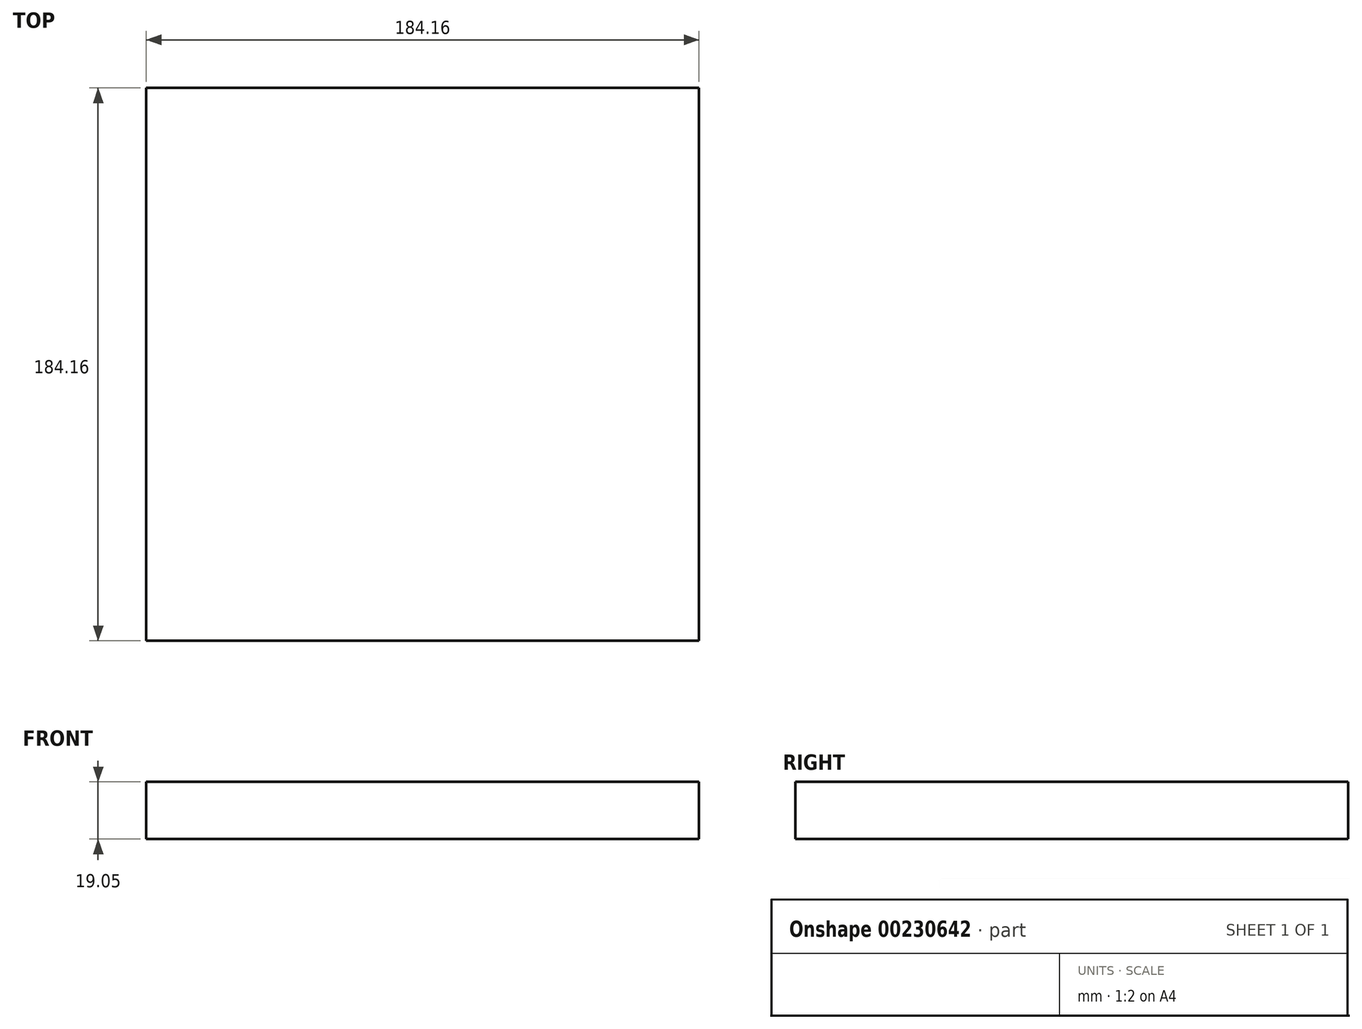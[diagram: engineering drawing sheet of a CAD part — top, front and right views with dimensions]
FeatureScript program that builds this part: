
annotation { "Feature Type Name" : "Feature", "Feature Type Description" : "" }
export const myFeature = defineFeature(function(context is Context, id is Id, definition is map)
    precondition{}
    {
        {
            var Q0;
            Q0=qCreatedBy(makeId("Top.planeOp"),FACE);
            var sketch = newSketch(context, id + "F0", { "sketchPlane" : qUnion([Q0])});
            skLineSegment(sketch, "E0.bottom", {"start": v(92.07, 92.08) * mm, "end": v(-92.07, 92.08) * mm});
            skLineSegment(sketch, "E0.top", {"start": v(92.08, -92.08) * mm, "end": v(-92.07, -92.08) * mm});
            skLineSegment(sketch, "E0.left", {"start": v(92.08, 92.08) * mm, "end": v(92.08, -92.08) * mm});
            skLineSegment(sketch, "E0.right", {"start": v(-92.07, 92.08) * mm, "end": v(-92.07, -92.08) * mm});
            skPoint(sketch, "E0.middle", {"position": v(0, 0) * mm});
            skSolve(sketch);
        }
        {
            var Q0;
            Q0 = qSketchRegion(id + "F0", true);
            extrude(context, id + "F1", {"entities" : qUnion([Q0]), "depth" : 19.05 * mm});
        }
    });
